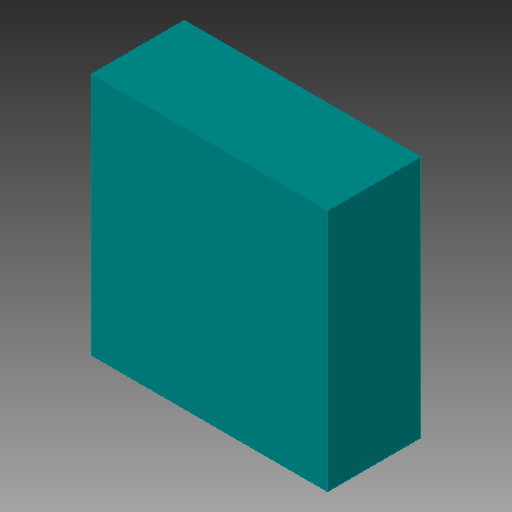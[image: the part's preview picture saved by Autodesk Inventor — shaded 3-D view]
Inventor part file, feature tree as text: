
AUTODESK INVENTOR PART (.ipt)
format: ipt  version: 2018 (Build 220112000, 112)  size: 80,384 bytes
history: native  units: in
note: dims shown in document units (in); Inventor stores cm internally (conversion verified against a paired STEP export)
features: other x1, extrude x1
ambient origin geometry x8: Origin, YZ Plane, XZ Plane, XY Plane, X Axis, Y Axis, Z Axis, Center Point
bodies: Solid1 (feature_tree)
feature tree (2):
  other  "1X01, 1X01_146"
  extrude  "Extrusion1"  Depth=0.0394in TaperAngle=0.0deg
